# Revit family: 2093130 Sylvania Lighting Fixture MC2 TRIM 2-4M 4K DALIEM WHT OPAL
name_source: partatom
category: Lighting Fixtures
revit_build: Autodesk Revit 2016 (Build: 20150220_1215(x64)
units: mm (PartAtom-declared; Revit-internal decimal feet)

## family parameters
Cut with Voids When Loaded = No
Host = Face
Light Source = Yes
OmniClass Number = 23.80.70.11.17
OmniClass Title = Specialized Lighting by Location or Use
Part Type = Normal
Room Calculation Point = No
Round Connector Dimension = Use Diameter
Shared = No

## types (2) — shared parameters
Apparent Load = 45 VA
Assembly Code = D5020200
AssetType = Fixed
Color Filter = 16777215
Description = Mini Continuum II introduces a uniquely clean, simple LED lighting system offering continuous, highly uniform lines of light across walls and ceilings. This highly versatile lighting tool can be recessed, semi-recessed, surface-mounted or suspended, either vertically or horizontally. Available as direct/indirect or direct only distribution - both of which can be interconnected. Every batten has a plug and socket arrangement for easy and rapid electrical installation. Mini Continuum II Direct is available in two versions: one with an outside trim detail for plasterboard ceilings; and a trimless version for when a seamless effect is required. Dimmable DALI versions and 3hr non-maintained integral emergency options are available as standard options
Dimming Lamp Color Temperature Shift = <None>
DocumentationLiterature = http://www.sylvania-lighting.com
DurationUnit = hours
ElectricShockClassification = Class I
Emit Shape Visible in Rendering = No
Emit from Rectangle Length = 2400 mm  [stored 7.87402 ft]
Emit from Rectangle Width = 52 mm  [stored 0.170604 ft]
ExpectedLife = 50000
Height_SYL = 86 mm  [stored 0.282152 ft]
IfcExportAs = IfcLightFixtureType
IfcExportType = IfcLightFixtureType
IngressProtection = IP20
Keynote = 16500
Lamp = LED
LampColourRenderingIndex = 80
LampColourTemperature = 4000 K
LampMacAdamStep = 3
LampsType = LED
Length_SYL = 2400 mm  [stored 7.87402 ft]
LightOutputRatio = 100
Manufacturer = Feilo Sylvania
ManufacturerName = Feilo Sylvania
Material = aluminium housing, polycarbonate diffuser
Material_1_SYL = Metal_Sylvania_Mini Continuum II_White
Material_2_SYL = Polycarbonate_Sylvania_Mini Continuum II_Opal_4000K
Material_3_SYL = Metal_Sylvania_Mini Contiuum II_Silver
Model = MC2 TRIM 2.4M 4K DALIEM WHT OPAL
ModelNumber = 2093130
ModelReference = MC2 TRIM 2.4M 4K DALIEM WHT OPAL
NominalHeight = 86 mm  [stored 0.282152 ft]
NominalLength = 2400 mm  [stored 7.87402 ft]
PowerConsumption = 45 W
PowerFactor = 0.98
Tilt Angle = -90.00°
URL = http://www.sylvania-lighting.com
Voltage = 0 V
Weight = 5.9 kg
Width_SYL = 54 mm  [stored 0.177165 ft]
zero-valued in all types: Default Elevation, NominalWidth

## per-type parameters (varying)
| type | LampNominalLuminous | LuminousEfficacy | Name | Photometric Web File | TypeName |
| 2093130 MC2 TRIM 2.4M 4K DALIEM WHT OPAL Emergency mode | 121 lm | 2.688 lm/W | MC2 TRIM 2.4M 4K DALIEM WHT OPAL Emergency mode | 2093130EM.ies | MC2 TRIM 2.4M 4K DALIEM WHT OPAL Emergency mode |
| 2093130 MC2 TRIM 2.4M 4K DALIEM WHT OPAL | 4680 lm | 104 lm/W | MC2 TRIM 2.4M 4K DALIEM WHT OPAL | 2093130.ies | MC2 TRIM 2.4M 4K DALIEM WHT OPAL |

note: [stored X ft] marks values corroborated as IEEE doubles in the binary element streams (Revit-internal decimal feet)

## geometry (parser evidence)
native form markers: Sweep x2
no freeform markers — native parametric forms only
